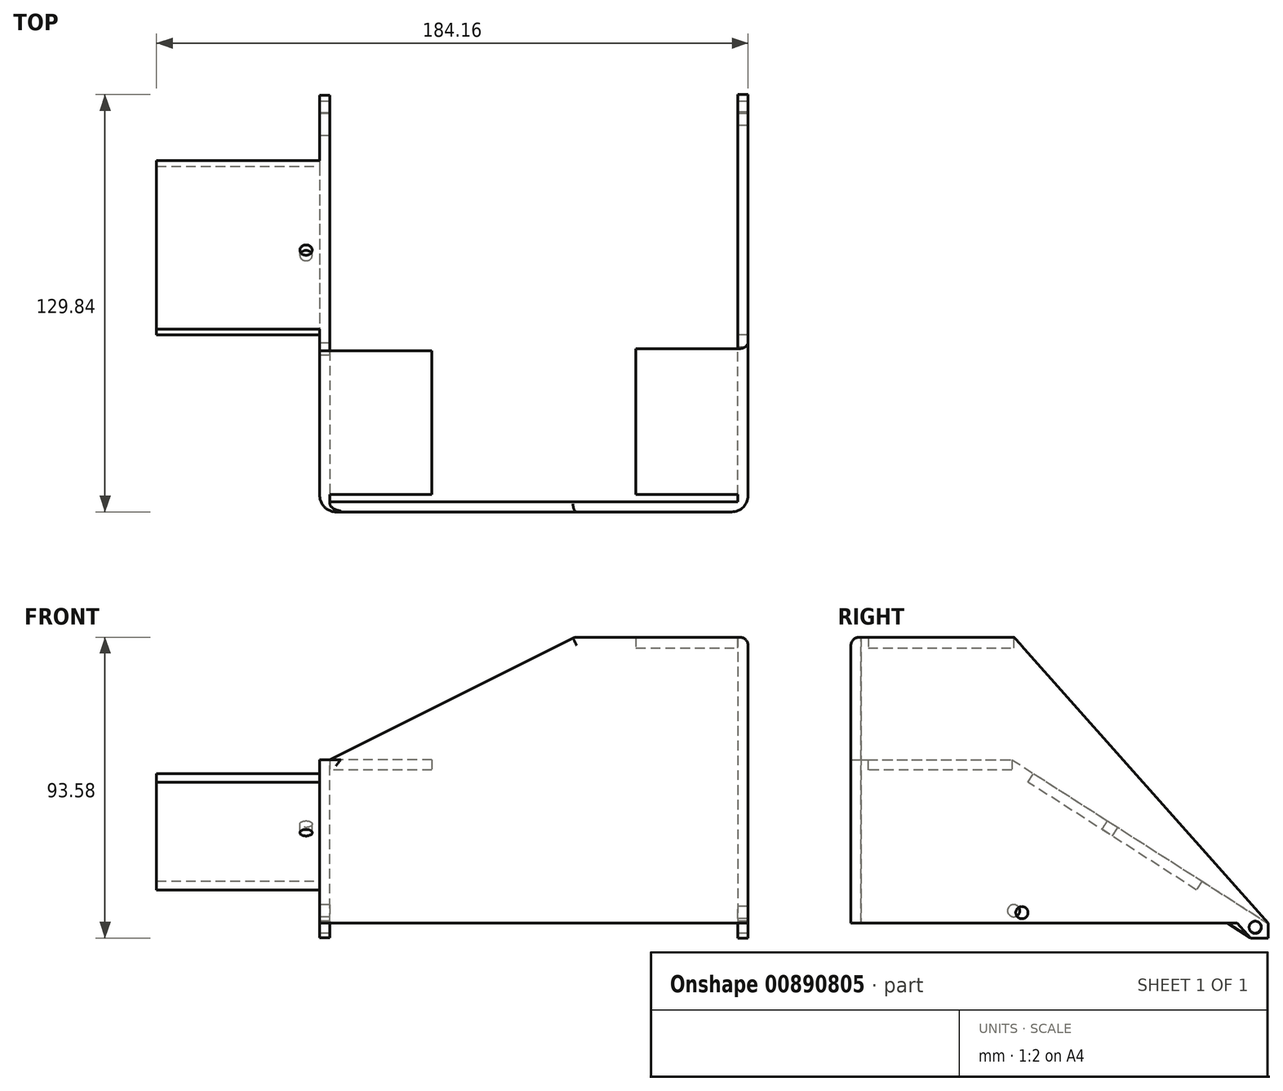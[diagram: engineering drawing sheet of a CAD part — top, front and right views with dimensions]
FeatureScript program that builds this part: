
annotation { "Feature Type Name" : "Feature", "Feature Type Description" : "" }
export const myFeature = defineFeature(function(context is Context, id is Id, definition is map)
    precondition{}
    {
        {
            var Q0;
            Q0=qCreatedBy(makeId("Front.planeOp"),FACE);
            var sketch = newSketch(context, id + "F0", { "sketchPlane" : qUnion([Q0])});
            skLineSegment(sketch, "E0", {"start": v(0, 0) * mm, "end": v(-76.2, 0) * mm});
            skLineSegment(sketch, "E1", {"start": v(-76.2, 0) * mm, "end": v(-76.2, 50.8) * mm});
            skLineSegment(sketch, "E2", {"start": v(0, 88.9) * mm, "end": v(50.8, 88.9) * mm});
            skLineSegment(sketch, "E3", {"start": v(50.8, 88.9) * mm, "end": v(50.8, 0) * mm});
            skLineSegment(sketch, "E4", {"start": v(50.8, 0) * mm, "end": v(0, 0) * mm});
            skLineSegment(sketch, "E5", {"start": v(-76.2, 50.8) * mm, "end": v(0, 88.9) * mm});
            skSolve(sketch);
        }
        {
            var Q0;
            Q0 = qSketchRegion(id + "F0", true);
            extrude(context, id + "F1", {"entities" : qUnion([Q0]), "depth" : 3.17 * mm, "offsetDistance" : 25.4 * mm});
        }
        {
            var Q0;
            Q0=makeQuery(id+"F1.opExtrude","SWEPT_FACE",FACE,{"disambiguationData":[OSD([sQuery(id+"F0.wireOp",EDGE,"E3")])]});
            var sketch = newSketch(context, id + "F2", { "sketchPlane" : qUnion([Q0])});
            skLineSegment(sketch, "E6", {"start": v(-3.18, 88.9) * mm, "end": v(47.62, 88.9) * mm});
            skLineSegment(sketch, "E7", {"start": v(47.62, 88.9) * mm, "end": v(126.66, 0) * mm});
            skLineSegment(sketch, "E8", {"start": v(126.66, 0) * mm, "end": v(126.66, -4.68) * mm});
            skLineSegment(sketch, "E9", {"start": v(126.66, -4.68) * mm, "end": v(121.25, -4.68) * mm});
            skLineSegment(sketch, "E10", {"start": v(121.25, -4.68) * mm, "end": v(117.05, 0) * mm});
            skLineSegment(sketch, "E11", {"start": v(117.05, 0) * mm, "end": v(-3.17, 0) * mm});
            skLineSegment(sketch, "E12", {"start": v(-3.17, 0) * mm, "end": v(-3.18, 88.9) * mm});
            skCircle(sketch, "E13", {"center": v(122.67, -1.35) * mm, "radius": 1.9 * mm});
            skCircle(sketch, "E14", {"center": v(50.03, 3.21) * mm, "radius": 1.9 * mm});
            skSolve(sketch);
        }
        {
            var Q0;
            Q0 = qSketchRegion(id + "F2", true);
            extrude(context, id + "F3", {"entities" : qUnion([Q0]), "operationType" : NewBodyOperationType.ADD, "depth" : 3.17 * mm, "offsetDistance" : 25.4 * mm});
        }
        {
            var Q0;
            Q0=makeQuery(id+"F3.opExtrude","CAP_EDGE",EDGE,{"disambiguationData":[OSD([sQuery(id+"F2.wireOp",EDGE,"E12")])],"isStart":false});
            fillet(context, id + "F4", {"entities" : qUnion([Q0]), "radius" : 5.08 * mm, "tangentPropagation" : true, "allowEdgeOverflow" : false});
        }
        {
            var Q0;
            Q0=makeQuery(id+"F3.opExtrude","CAP_FACE",FACE,{"disambiguationData":[OSD([sQuery(id+"F2.wireOp",EDGE,"E6"),sQuery(id+"F2.wireOp",EDGE,"E7"),sQuery(id+"F2.wireOp",EDGE,"E8"),sQuery(id+"F2.wireOp",EDGE,"E9"),sQuery(id+"F2.wireOp",EDGE,"E10"),sQuery(id+"F2.wireOp",EDGE,"E11"),sQuery(id+"F2.wireOp",EDGE,"E12")])],"isStart":true});
            var sketch = newSketch(context, id + "F5", { "sketchPlane" : qUnion([Q0])});
            skLineSegment(sketch, "E15", {"start": v(-47.62, 88.9) * mm, "end": v(-2.2, 88.9) * mm});
            skLineSegment(sketch, "E16", {"start": v(-2.2, 88.9) * mm, "end": v(-2.2, 85.56) * mm});
            skLineSegment(sketch, "E17", {"start": v(-2.2, 85.56) * mm, "end": v(-47.62, 85.56) * mm});
            skLineSegment(sketch, "E18", {"start": v(-47.62, 85.56) * mm, "end": v(-47.62, 88.9) * mm});
            skSolve(sketch);
        }
        {
            var Q0;
            Q0 = qSketchRegion(id + "F5", true);
            extrude(context, id + "F6", {"entities" : qUnion([Q0]), "operationType" : NewBodyOperationType.ADD, "depth" : 31.75 * mm, "offsetDistance" : 25.4 * mm});
        }
        {
            var Q0;
            Q0=makeQuery(id+"F1.opExtrude","SWEPT_FACE",FACE,{"disambiguationData":[OSD([sQuery(id+"F0.wireOp",EDGE,"E1")])]});
            var sketch = newSketch(context, id + "F7", { "sketchPlane" : qUnion([Q0])});
            skLineSegment(sketch, "E19", {"start": v(-126.44, 0) * mm, "end": v(-126.44, -4.56) * mm});
            skLineSegment(sketch, "E20", {"start": v(-126.44, -4.56) * mm, "end": v(-121.14, -4.56) * mm});
            skLineSegment(sketch, "E21", {"start": v(3.17, 0) * mm, "end": v(3.18, 50.8) * mm});
            skLineSegment(sketch, "E22", {"start": v(3.18, 50.8) * mm, "end": v(-46.9, 50.8) * mm});
            skLineSegment(sketch, "E23", {"start": v(-46.9, 50.8) * mm, "end": v(-126.44, 0) * mm});
            skLineSegment(sketch, "E24", {"start": v(-121.14, -4.56) * mm, "end": v(-114, 0) * mm});
            skLineSegment(sketch, "E25", {"start": v(-114, 0) * mm, "end": v(3.17, 0) * mm});
            skSolve(sketch);
        }
        {
            var Q0;
            Q0 = qSketchRegion(id + "F7", true);
            extrude(context, id + "F8", {"entities" : qUnion([Q0]), "operationType" : NewBodyOperationType.ADD, "depth" : 3.17 * mm, "offsetDistance" : 25.4 * mm});
        }
        {
            var Q0;
            Q0=makeQuery(id+"F8.opExtrude","CAP_FACE",FACE,{"disambiguationData":[OSD([sQuery(id+"F7.wireOp",EDGE,"E19"),sQuery(id+"F7.wireOp",EDGE,"E20"),sQuery(id+"F7.wireOp",EDGE,"E21"),sQuery(id+"F7.wireOp",EDGE,"E22"),sQuery(id+"F7.wireOp",EDGE,"E23"),sQuery(id+"F7.wireOp",EDGE,"E24"),sQuery(id+"F7.wireOp",EDGE,"E25")])],"isStart":true});
            var sketch = newSketch(context, id + "F9", { "sketchPlane" : qUnion([Q0])});
            skLineSegment(sketch, "E26", {"start": v(2.2, 50.8) * mm, "end": v(46.9, 50.8) * mm});
            skLineSegment(sketch, "E27", {"start": v(46.9, 50.8) * mm, "end": v(46.9, 47.62) * mm});
            skLineSegment(sketch, "E28", {"start": v(46.9, 47.62) * mm, "end": v(2.2, 47.62) * mm});
            skLineSegment(sketch, "E29", {"start": v(2.2, 47.62) * mm, "end": v(2.2, 50.8) * mm});
            skSolve(sketch);
        }
        {
            var Q0;
            Q0 = qSketchRegion(id + "F9", true);
            extrude(context, id + "F10", {"entities" : qUnion([Q0]), "operationType" : NewBodyOperationType.ADD, "depth" : 31.75 * mm, "offsetDistance" : 25.4 * mm});
        }
        {
            var Q0;
            Q0=makeQuery(id+"F8.opExtrude","CAP_EDGE",EDGE,{"disambiguationData":[OSD([sQuery(id+"F7.wireOp",EDGE,"E21")])],"isStart":false});
            fillet(context, id + "F11", {"entities" : qUnion([Q0]), "radius" : 5.08 * mm, "tangentPropagation" : true, "allowEdgeOverflow" : false});
        }
        {
            var Q0;
            Q0=makeQuery(id+"F8.opExtrude","CAP_FACE",FACE,{"disambiguationData":[OSD([sQuery(id+"F7.wireOp",EDGE,"E19"),sQuery(id+"F7.wireOp",EDGE,"E20"),sQuery(id+"F7.wireOp",EDGE,"E21"),sQuery(id+"F7.wireOp",EDGE,"E22"),sQuery(id+"F7.wireOp",EDGE,"E23"),sQuery(id+"F7.wireOp",EDGE,"E24"),sQuery(id+"F7.wireOp",EDGE,"E25")])],"isStart":false});
            var sketch = newSketch(context, id + "F12", { "sketchPlane" : qUnion([Q0])});
            skLineSegment(sketch, "E30", {"start": v(-53.66, 46.49) * mm, "end": v(-106.1, 12.99) * mm});
            skLineSegment(sketch, "E31", {"start": v(-106.1, 12.99) * mm, "end": v(-104.4, 10.31) * mm});
            skLineSegment(sketch, "E32", {"start": v(-104.4, 10.31) * mm, "end": v(-51.95, 43.81) * mm});
            skLineSegment(sketch, "E33", {"start": v(-51.95, 43.81) * mm, "end": v(-53.66, 46.49) * mm});
            skSolve(sketch);
        }
        {
            var Q0;
            Q0 = qSketchRegion(id + "F12", true);
            extrude(context, id + "F13", {"entities" : qUnion([Q0]), "operationType" : NewBodyOperationType.ADD, "depth" : 50.8 * mm, "offsetDistance" : 25.4 * mm});
        }
        {
            var Q0;
            Q0=makeQuery(id+"F8.opExtrude","CAP_FACE",FACE,{"disambiguationData":[OSD([sQuery(id+"F7.wireOp",EDGE,"E19"),sQuery(id+"F7.wireOp",EDGE,"E20"),sQuery(id+"F7.wireOp",EDGE,"E21"),sQuery(id+"F7.wireOp",EDGE,"E22"),sQuery(id+"F7.wireOp",EDGE,"E23"),sQuery(id+"F7.wireOp",EDGE,"E24"),sQuery(id+"F7.wireOp",EDGE,"E25")])],"isStart":false});
            var sketch = newSketch(context, id + "F14", { "sketchPlane" : qUnion([Q0])});
            skCircle(sketch, "E34", {"center": v(-122.63, -1.26) * mm, "radius": 1.9 * mm});
            skCircle(sketch, "E35", {"center": v(-47.48, 3.81) * mm, "radius": 1.9 * mm});
            skSolve(sketch);
        }
        {
            var Q0;
            Q0 = qSketchRegion(id + "F14", true);
            extrude(context, id + "F15", {"entities" : qUnion([Q0]), "operationType" : NewBodyOperationType.REMOVE, "oppositeDirection" : true, "depth" : 25.4 * mm, "offsetDistance" : 25.4 * mm});
        }
        {
            var Q0;
            Q0=makeQuery(id+"F13.boolean.opBoolean","MERGE",FACE,{"derivedFrom":[makeQuery(id+"F8.opExtrude","SWEPT_FACE",FACE,{"disambiguationData":[OSD([sQuery(id+"F7.wireOp",EDGE,"E23")])]}),makeQuery(id+"F13.opExtrude","SWEPT_FACE",FACE,{"disambiguationData":[OSD([sQuery(id+"F12.wireOp",EDGE,"E30")])]})]});
            var sketch = newSketch(context, id + "F16", { "sketchPlane" : qUnion([Q0])});
            skCircle(sketch, "E36", {"center": v(-83.64, 49.4) * mm, "radius": 1.9 * mm});
            skSolve(sketch);
        }
        {
            var Q0;
            Q0 = qSketchRegion(id + "F16", true);
            extrude(context, id + "F17", {"entities" : qUnion([Q0]), "operationType" : NewBodyOperationType.REMOVE, "oppositeDirection" : true, "depth" : 25.4 * mm, "offsetDistance" : 25.4 * mm});
        }
        {
            var Q0;
            Q0=makeQuery(id+"F1.opExtrude","CAP_EDGE",EDGE,{"disambiguationData":[OSD([sQuery(id+"F0.wireOp",EDGE,"E5")])],"isStart":false});
            fillet(context, id + "F18", {"entities" : qUnion([Q0]), "radius" : 2.54 * mm, "tangentPropagation" : true, "allowEdgeOverflow" : false});
        }
        {
            var Q0;
            Q0=makeQuery(id+"F3.boolean.opBoolean","MERGE",EDGE,{"derivedFrom":[makeQuery(id+"F1.opExtrude","CAP_EDGE",EDGE,{"disambiguationData":[OSD([sQuery(id+"F0.wireOp",EDGE,"E2")])],"isStart":false}),makeQuery(id+"F3.opExtrude","SWEPT_EDGE",EDGE,{"disambiguationData":[OSD([sQuery(id+"F2.wireOp",EDGE,"E6"),sQuery(id+"F2.wireOp",EDGE,"E12")])]})]});
            fillet(context, id + "F19", {"entities" : qUnion([Q0]), "radius" : 2.54 * mm, "tangentPropagation" : true, "allowEdgeOverflow" : false});
        }
    });
